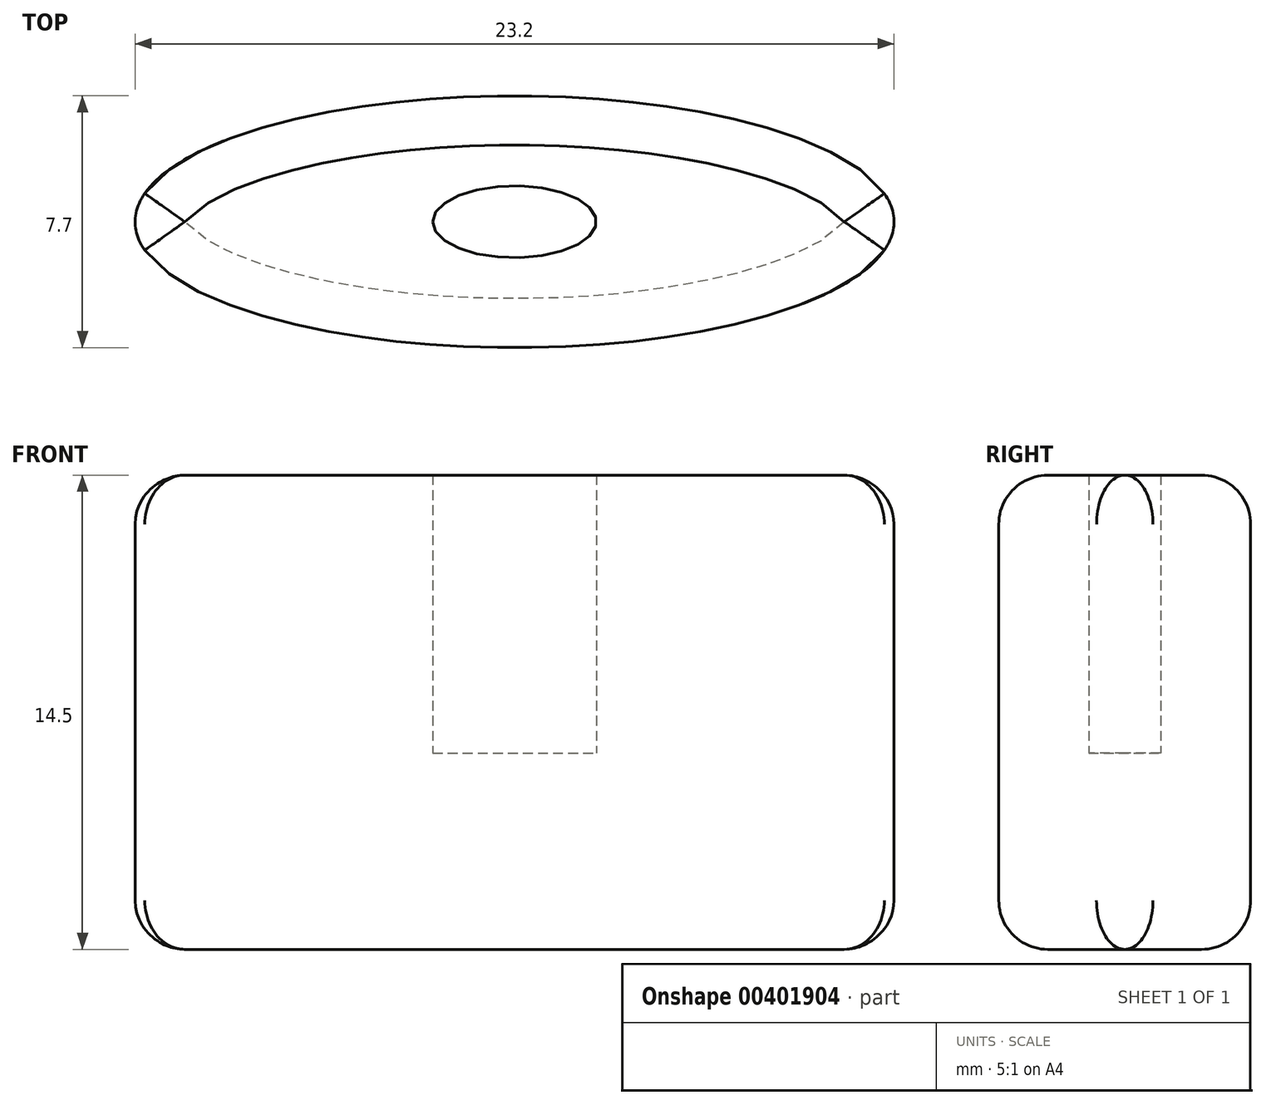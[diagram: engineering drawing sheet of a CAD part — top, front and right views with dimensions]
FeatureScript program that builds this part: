
annotation { "Feature Type Name" : "Feature", "Feature Type Description" : "" }
export const myFeature = defineFeature(function(context is Context, id is Id, definition is map)
    precondition{}
    {
        {
            var Q0;
            Q0=qCreatedBy(makeId("Top.planeOp"),FACE);
            var sketch = newSketch(context, id + "F0", { "sketchPlane" : qUnion([Q0])});
            skEllipse(sketch, "E0", {"center": v(0, 0) * mm, "majorRadius": 11.6 * mm, "minorRadius": 3.85 * mm, "majorAxis": v(-1, 0)});
            skEllipse(sketch, "E1", {"center": v(0, 0) * mm, "majorRadius": 2.5 * mm, "minorRadius": 1.1 * mm, "majorAxis": v(-1, 0)});
            skSolve(sketch);
        }
        {
            var Q0;
            Q0=makeQuery(id+"F0.imprint","IMPRINT",FACE,{"disambiguationData":[TD([[makeQuery(id+"F0.imprint","IMPRINT",EDGE,{"derivedFrom":sQuery(id+"F0.wireOp",EDGE,"E0")}),1.0]])]});
            extrude(context, id + "F1", {"entities" : qUnion([Q0]), "depth" : 8.5 * mm});
        }
        {
            var Q0;
            Q0=makeQuery(id+"F0.imprint","IMPRINT",FACE,{"disambiguationData":[TD([[makeQuery(id+"F0.imprint","IMPRINT",EDGE,{"derivedFrom":sQuery(id+"F0.wireOp",EDGE,"E1")}),1.0]])]});
            var Q1;
            Q1=makeQuery(id+"F1.opExtrude","CAP_FACE",FACE,{"disambiguationData":[OSD([sQuery(id+"F0.wireOp",EDGE,"E0"),sQuery(id+"F0.wireOp",EDGE,"E1")])],"isStart":true});
            extrude(context, id + "F2", {"entities" : qUnion([Q0, Q1]), "operationType" : NewBodyOperationType.ADD, "oppositeDirection" : true, "depth" : 6 * mm});
        }
        {
            var Q0;
            Q0=makeQuery(id+"F2.opExtrude","CAP_EDGE",EDGE,{"disambiguationData":[OSD([sQuery(id+"F0.wireOp",EDGE,"E0")])],"isStart":false});
            var Q1;
            Q1=makeQuery(id+"F1.opExtrude","CAP_EDGE",EDGE,{"disambiguationData":[OSD([sQuery(id+"F0.wireOp",EDGE,"E0")])],"isStart":false});
            fillet(context, id + "F3", {"entities" : qUnion([Q0, Q1]), "radius" : 1.5 * mm, "allowEdgeOverflow" : false});
        }
    });
